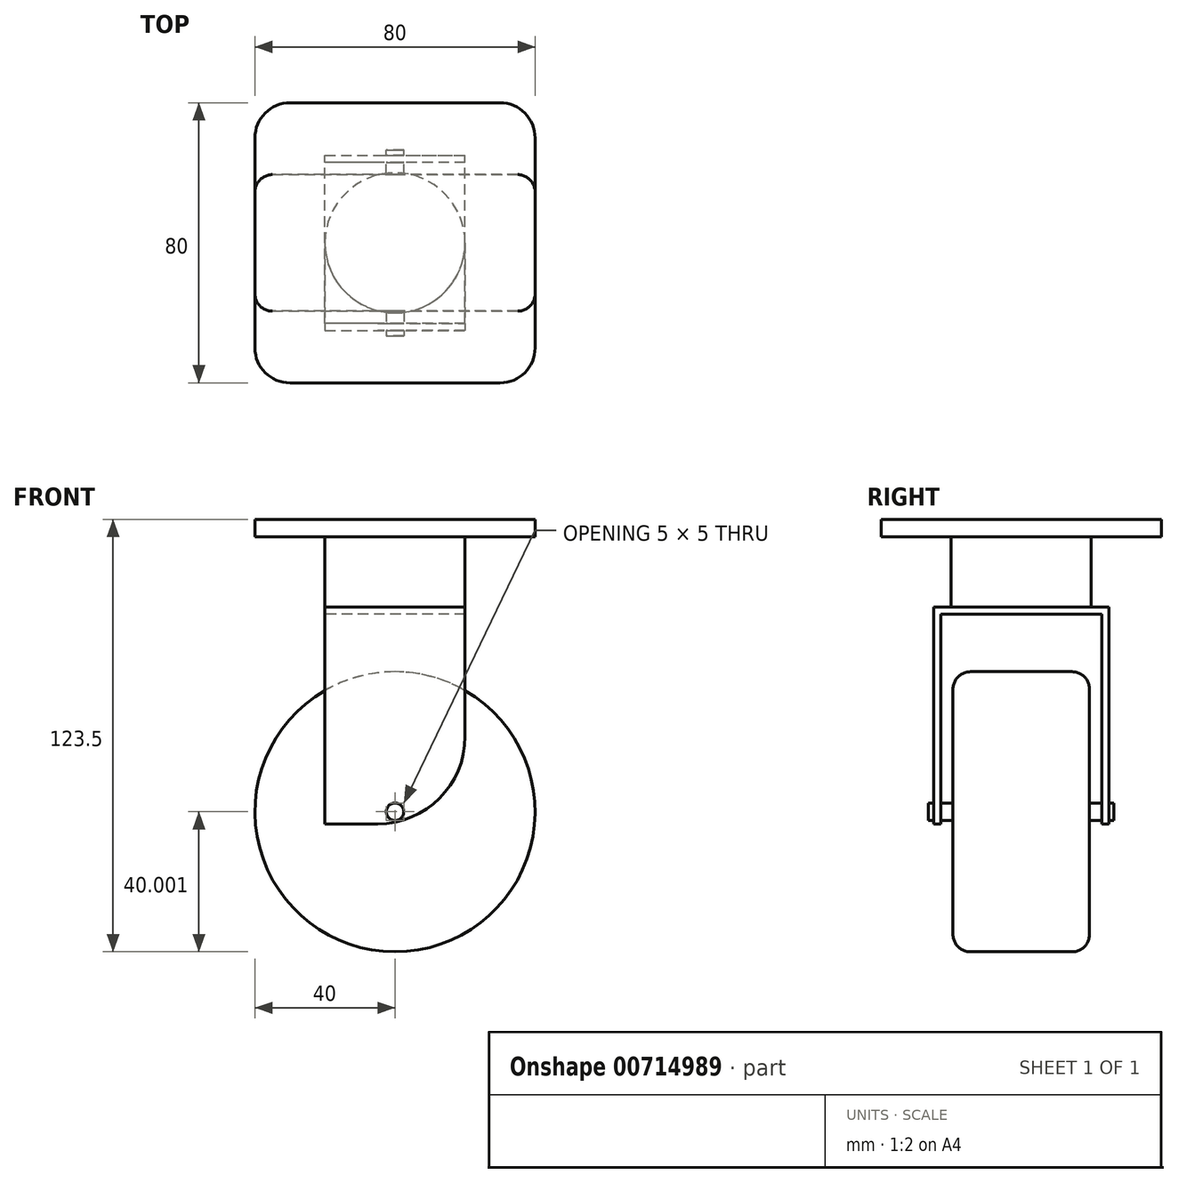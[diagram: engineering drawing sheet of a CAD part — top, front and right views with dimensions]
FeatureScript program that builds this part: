
annotation { "Feature Type Name" : "Feature", "Feature Type Description" : "" }
export const myFeature = defineFeature(function(context is Context, id is Id, definition is map)
    precondition{}
    {
        {
            var Q0;
            Q0=qCreatedBy(makeId("Front.planeOp"),FACE);
            var sketch = newSketch(context, id + "F0", { "sketchPlane" : qUnion([Q0])});
            skLineSegment(sketch, "E0.bottom", {"start": v(-40, 42.5) * mm, "end": v(40, 42.5) * mm});
            skLineSegment(sketch, "E0.top", {"start": v(-40, 37.5) * mm, "end": v(40, 37.5) * mm});
            skLineSegment(sketch, "E0.left", {"start": v(-40, 42.5) * mm, "end": v(-40, 37.5) * mm});
            skLineSegment(sketch, "E0.right", {"start": v(40, 42.5) * mm, "end": v(40, 37.5) * mm});
            skSolve(sketch);
        }
        {
            var Q0;
            Q0=makeQuery(id+"F0.imprint","IMPRINT",FACE,{"disambiguationData":[TD([[makeQuery(id+"F0.imprint","IMPRINT",EDGE,{"derivedFrom":sQuery(id+"F0.wireOp",EDGE,"E0.bottom")}),-1.0]])]});
            extrude(context, id + "F1", {"entities" : qUnion([Q0]), "oppositeDirection" : true, "depth" : 40 * mm, "offsetDistance" : 25 * mm});
        }
        {
            var Q0;
            Q0=makeQuery(id+"F1.opExtrude","SWEPT_FACE",FACE,{"disambiguationData":[OSD([sQuery(id+"F0.wireOp",EDGE,"E0.top")])]});
            var sketch = newSketch(context, id + "F2", { "sketchPlane" : qUnion([Q0])});
            skArc(sketch, "E1", {"start": v(-20, 0) * mm, "mid": v(0, -20) * mm, "end": v(20, 0) * mm});
            skLineSegment(sketch, "E2", {"start": v(-20, 0) * mm, "end": v(20, 0) * mm});
            skSolve(sketch);
        }
        {
            var Q0;
            Q0=makeQuery(id+"F2.imprint","IMPRINT",FACE,{"disambiguationData":[TD([[makeQuery(id+"F2.imprint","IMPRINT",EDGE,{"derivedFrom":sQuery(id+"F2.wireOp",EDGE,"E1")}),1.0]])]});
            extrude(context, id + "F3", {"entities" : qUnion([Q0]), "operationType" : NewBodyOperationType.ADD, "depth" : 20 * mm, "offsetDistance" : 25 * mm});
        }
        {
            var Q0;
            Q0=makeQuery(id+"F3.opExtrude","CAP_FACE",FACE,{"disambiguationData":[OSD([sQuery(id+"F2.wireOp",EDGE,"E1"),sQuery(id+"F2.wireOp",EDGE,"E2")])],"isStart":false});
            var sketch = newSketch(context, id + "F4", { "sketchPlane" : qUnion([Q0])});
            skLineSegment(sketch, "E3.bottom", {"start": v(-20, 0) * mm, "end": v(20, 0) * mm});
            skLineSegment(sketch, "E3.top", {"start": v(-20, -25) * mm, "end": v(20, -25) * mm});
            skLineSegment(sketch, "E3.left", {"start": v(-20, 0) * mm, "end": v(-20, -25) * mm});
            skLineSegment(sketch, "E3.right", {"start": v(20, 0) * mm, "end": v(20, -25) * mm});
            skSolve(sketch);
        }
        {
            var Q0;
            Q0=makeQuery(id+"F4.imprint","IMPRINT",FACE,{"disambiguationData":[TD([[makeQuery(id+"F4.imprint","IMPRINT",EDGE,{"derivedFrom":sQuery(id+"F4.wireOp",EDGE,"E3.top")}),1.0]])]});
            var Q1;
            Q1=makeQuery(id+"F4.imprint","IMPRINT",FACE,{"disambiguationData":[TD([[makeQuery(id+"F4.imprint","IMPRINT",EDGE,{"derivedFrom":sQuery(id+"F4.wireOp",EDGE,"E3.bottom")}),-1.0]])]});
            extrude(context, id + "F5", {"entities" : qUnion([Q0, Q1]), "operationType" : NewBodyOperationType.ADD, "depth" : 2 * mm, "offsetDistance" : 25 * mm});
        }
        {
            var Q0;
            Q0=makeQuery(id+"F5.opExtrude","CAP_FACE",FACE,{"disambiguationData":[OSD([sQuery(id+"F4.wireOp",EDGE,"E3.bottom"),sQuery(id+"F4.wireOp",EDGE,"E3.top"),sQuery(id+"F4.wireOp",EDGE,"E3.left"),sQuery(id+"F4.wireOp",EDGE,"E3.right")])],"isStart":false});
            var sketch = newSketch(context, id + "F6", { "sketchPlane" : qUnion([Q0])});
            skLineSegment(sketch, "E4.bottom", {"start": v(20, -23) * mm, "end": v(-20, -23) * mm});
            skLineSegment(sketch, "E4.top", {"start": v(20, -25) * mm, "end": v(-20, -25) * mm});
            skLineSegment(sketch, "E4.left", {"start": v(20, -23) * mm, "end": v(20, -25) * mm});
            skLineSegment(sketch, "E4.right", {"start": v(-20, -23) * mm, "end": v(-20, -25) * mm});
            skSolve(sketch);
        }
        {
            var Q0;
            Q0=makeQuery(id+"F6.imprint","IMPRINT",FACE,{"disambiguationData":[TD([[makeQuery(id+"F6.imprint","IMPRINT",EDGE,{"derivedFrom":sQuery(id+"F6.wireOp",EDGE,"E4.bottom")}),1.0]])]});
            extrude(context, id + "F7", {"entities" : qUnion([Q0]), "operationType" : NewBodyOperationType.ADD, "depth" : 60 * mm, "offsetDistance" : 25 * mm});
        }
        {
            var Q0;
            Q0=makeQuery(id+"F7.opExtrude","SWEPT_FACE",FACE,{"disambiguationData":[OSD([sQuery(id+"F6.wireOp",EDGE,"E4.bottom")])]});
            var sketch = newSketch(context, id + "F8", { "sketchPlane" : qUnion([Q0])});
            skCircle(sketch, "E5", {"center": v(0, -41) * mm, "radius": 2.5 * mm});
            skPoint(sketch, "E5.centerSnap0", {"position": v(0, -44.5) * mm});
            skSolve(sketch);
        }
        {
            var Q0;
            Q0=makeQuery(id+"F8.imprint","IMPRINT",FACE,{"disambiguationData":[TD([[makeQuery(id+"F8.imprint","IMPRINT",EDGE,{"derivedFrom":sQuery(id+"F8.wireOp",EDGE,"E5")}),1.0]])]});
            extrude(context, id + "F9", {"entities" : qUnion([Q0]), "operationType" : NewBodyOperationType.ADD, "endBound" : BoundingType.SYMMETRIC, "depth" : 7 * mm, "offsetDistance" : 25 * mm});
        }
        {
            var Q0;
            Q0=makeQuery(id+"F9.opExtrude","CAP_FACE",FACE,{"disambiguationData":[OSD([sQuery(id+"F8.wireOp",EDGE,"E5")])],"isStart":false});
            var sketch = newSketch(context, id + "F10", { "sketchPlane" : qUnion([Q0])});
            skCircle(sketch, "E6", {"center": v(0, -41) * mm, "radius": 40 * mm});
            skSolve(sketch);
        }
        {
            var Q0;
            Q0=makeQuery(id+"F10.imprint","IMPRINT",FACE,{"disambiguationData":[TD([[makeQuery(id+"F10.imprint","IMPRINT",EDGE,{"derivedFrom":makeQuery(id+"F9.opExtrude","CAP_EDGE",EDGE,{"disambiguationData":[OSD([sQuery(id+"F8.wireOp",EDGE,"E5")])],"isStart":false})}),1.0]])]});
            var Q1;
            Q1=makeQuery(id+"F10.imprint","IMPRINT",FACE,{"disambiguationData":[TD([[makeQuery(id+"F10.imprint","IMPRINT",EDGE,{"derivedFrom":sQuery(id+"F10.wireOp",EDGE,"E6")}),1.0]])]});
            var Q2;
            Q2=makeQuery(id+"F5.boolean.opBoolean","MERGE",FACE,{"derivedFrom":[makeQuery(id+"F3.boolean.opBoolean","MERGE",FACE,{"derivedFrom":[makeQuery(id+"F1.opExtrude","CAP_FACE",FACE,{"disambiguationData":[OSD([sQuery(id+"F0.wireOp",EDGE,"E0.bottom"),sQuery(id+"F0.wireOp",EDGE,"E0.top"),sQuery(id+"F0.wireOp",EDGE,"E0.left"),sQuery(id+"F0.wireOp",EDGE,"E0.right")])],"isStart":true}),makeQuery(id+"F3.opExtrude","SWEPT_FACE",FACE,{"disambiguationData":[OSD([sQuery(id+"F2.wireOp",EDGE,"E2")])]})]}),makeQuery(id+"F5.opExtrude","SWEPT_FACE",FACE,{"disambiguationData":[OSD([sQuery(id+"F4.wireOp",EDGE,"E3.bottom")])]})]});
            extrude(context, id + "F11", {"entities" : qUnion([Q0, Q1]), "operationType" : NewBodyOperationType.ADD, "endBound" : BoundingType.UP_TO_SURFACE, "depth" : 25 * mm, "endBoundEntityFace" : qUnion([Q2]), "offsetDistance" : 25 * mm});
        }
        {
            var Q0;
            Q0=makeQuery(id+"F1.opExtrude","SWEPT_BODY",BODY,{"disambiguationData":[OSD([sQuery(id+"F0.wireOp",EDGE,"E0.bottom"),sQuery(id+"F0.wireOp",EDGE,"E0.top"),sQuery(id+"F0.wireOp",EDGE,"E0.left"),sQuery(id+"F0.wireOp",EDGE,"E0.right")])]});
            var Q1;
            Q1=makeQuery(id+"F5.boolean.opBoolean","MERGE",FACE,{"derivedFrom":[makeQuery(id+"F3.boolean.opBoolean","MERGE",FACE,{"derivedFrom":[makeQuery(id+"F1.opExtrude","CAP_FACE",FACE,{"disambiguationData":[OSD([sQuery(id+"F0.wireOp",EDGE,"E0.bottom"),sQuery(id+"F0.wireOp",EDGE,"E0.top"),sQuery(id+"F0.wireOp",EDGE,"E0.left"),sQuery(id+"F0.wireOp",EDGE,"E0.right")])],"isStart":true}),makeQuery(id+"F3.opExtrude","SWEPT_FACE",FACE,{"disambiguationData":[OSD([sQuery(id+"F2.wireOp",EDGE,"E2")])]})]}),makeQuery(id+"F5.opExtrude","SWEPT_FACE",FACE,{"disambiguationData":[OSD([sQuery(id+"F4.wireOp",EDGE,"E3.bottom")])]})]});
            mirror(context, id + "F12", {"operationType" : NewBodyOperationType.ADD, "entities" : qUnion([Q0]), "mirrorPlane" : qUnion([Q1])});
        }
        {
            var Q0;
            Q0=makeQuery(id+"F11.opExtrude","CAP_EDGE",EDGE,{"disambiguationData":[OSD([sQuery(id+"F10.wireOp",EDGE,"E6")])],"isStart":true});
            var Q1;
            Q1=makeQuery(id+"F12.opPattern","COPY",EDGE,{"derivedFrom":makeQuery(id+"F11.opExtrude","CAP_EDGE",EDGE,{"disambiguationData":[OSD([sQuery(id+"F10.wireOp",EDGE,"E6")])],"isStart":true}),"instanceName":"1"});
            fillet(context, id + "F13", {"entities" : qUnion([Q0, Q1]), "radius" : 5 * mm, "tangentPropagation" : true, "allowEdgeOverflow" : false});
        }
        {
            var Q0;
            Q0=makeQuery(id+"F12.opPattern","COPY",EDGE,{"derivedFrom":makeQuery(id+"F1.opExtrude","CAP_EDGE",EDGE,{"disambiguationData":[OSD([sQuery(id+"F0.wireOp",EDGE,"E0.right")])],"isStart":false}),"instanceName":"1"});
            var Q1;
            Q1=makeQuery(id+"F12.opPattern","COPY",EDGE,{"derivedFrom":makeQuery(id+"F1.opExtrude","CAP_EDGE",EDGE,{"disambiguationData":[OSD([sQuery(id+"F0.wireOp",EDGE,"E0.left")])],"isStart":false}),"instanceName":"1"});
            var Q2;
            Q2=makeQuery(id+"F1.opExtrude","CAP_EDGE",EDGE,{"disambiguationData":[OSD([sQuery(id+"F0.wireOp",EDGE,"E0.left")])],"isStart":false});
            var Q3;
            Q3=makeQuery(id+"F1.opExtrude","CAP_EDGE",EDGE,{"disambiguationData":[OSD([sQuery(id+"F0.wireOp",EDGE,"E0.right")])],"isStart":false});
            fillet(context, id + "F14", {"entities" : qUnion([Q0, Q1, Q2, Q3]), "radius" : 10 * mm, "tangentPropagation" : true, "allowEdgeOverflow" : false});
        }
        {
            var Q0;
            Q0=makeQuery(id+"F7.opExtrude","CAP_EDGE",EDGE,{"disambiguationData":[OSD([sQuery(id+"F6.wireOp",EDGE,"E4.left")])],"isStart":false});
            fillet(context, id + "F15", {"entities" : qUnion([Q0]), "radius" : 25 * mm, "tangentPropagation" : true, "allowEdgeOverflow" : false});
        }
        {
            var Q0;
            Q0=makeQuery(id+"F12.opPattern","COPY",EDGE,{"derivedFrom":makeQuery(id+"F7.opExtrude","CAP_EDGE",EDGE,{"disambiguationData":[OSD([sQuery(id+"F6.wireOp",EDGE,"E4.left")])],"isStart":false}),"instanceName":"1"});
            fillet(context, id + "F16", {"entities" : qUnion([Q0]), "radius" : 25 * mm, "tangentPropagation" : true, "allowEdgeOverflow" : false});
        }
    });
